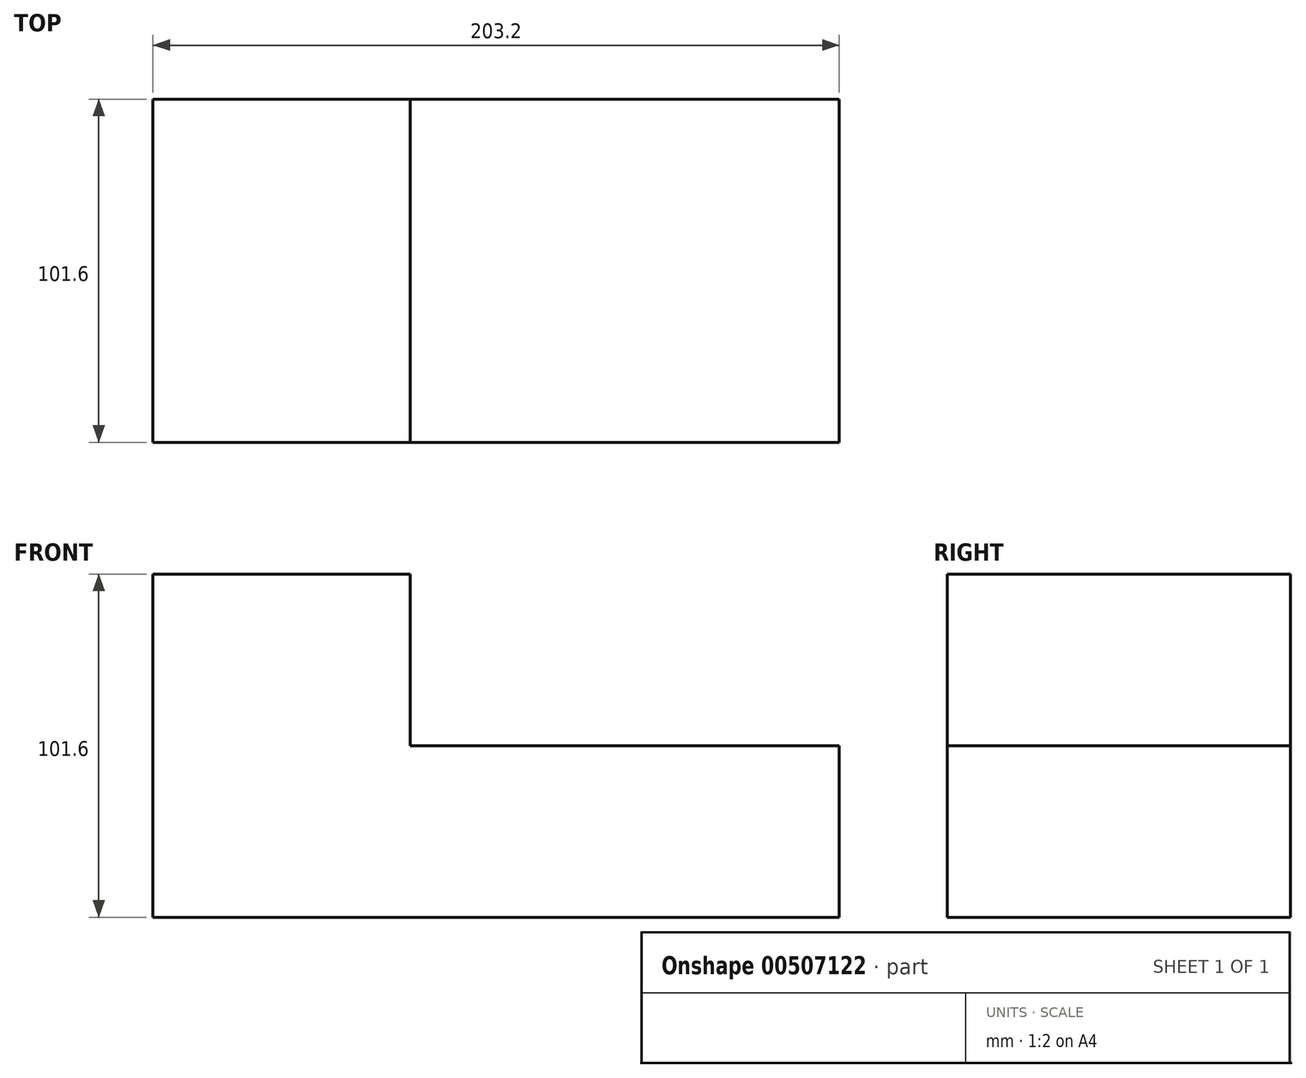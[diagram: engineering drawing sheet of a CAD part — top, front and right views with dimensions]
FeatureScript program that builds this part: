
annotation { "Feature Type Name" : "Feature", "Feature Type Description" : "" }
export const myFeature = defineFeature(function(context is Context, id is Id, definition is map)
    precondition{}
    {
        {
            var Q0;
            Q0=qCreatedBy(makeId("Front.planeOp"),FACE);
            var sketch = newSketch(context, id + "F0", { "sketchPlane" : qUnion([Q0])});
            skLineSegment(sketch, "E0.bottom", {"start": v(-63.82, -15.78) * mm, "end": v(12.38, -15.78) * mm});
            skLineSegment(sketch, "E0.top", {"start": v(-63.82, -117.38) * mm, "end": v(139.38, -117.38) * mm});
            skLineSegment(sketch, "E0.left", {"start": v(-63.82, -15.78) * mm, "end": v(-63.82, -117.38) * mm});
            skLineSegment(sketch, "E0.right", {"start": v(139.38, -66.58) * mm, "end": v(139.38, -117.38) * mm});
            skLineSegment(sketch, "E1.top", {"start": v(139.38, -66.58) * mm, "end": v(12.38, -66.58) * mm});
            skLineSegment(sketch, "E1.right", {"start": v(12.38, -15.78) * mm, "end": v(12.38, -66.58) * mm});
            skSolve(sketch);
        }
        {
            var Q0;
            Q0 = qSketchRegion(id + "F0", true);
            extrude(context, id + "F1", {"entities" : qUnion([Q0]), "depth" : 101.6 * mm});
        }
    });
